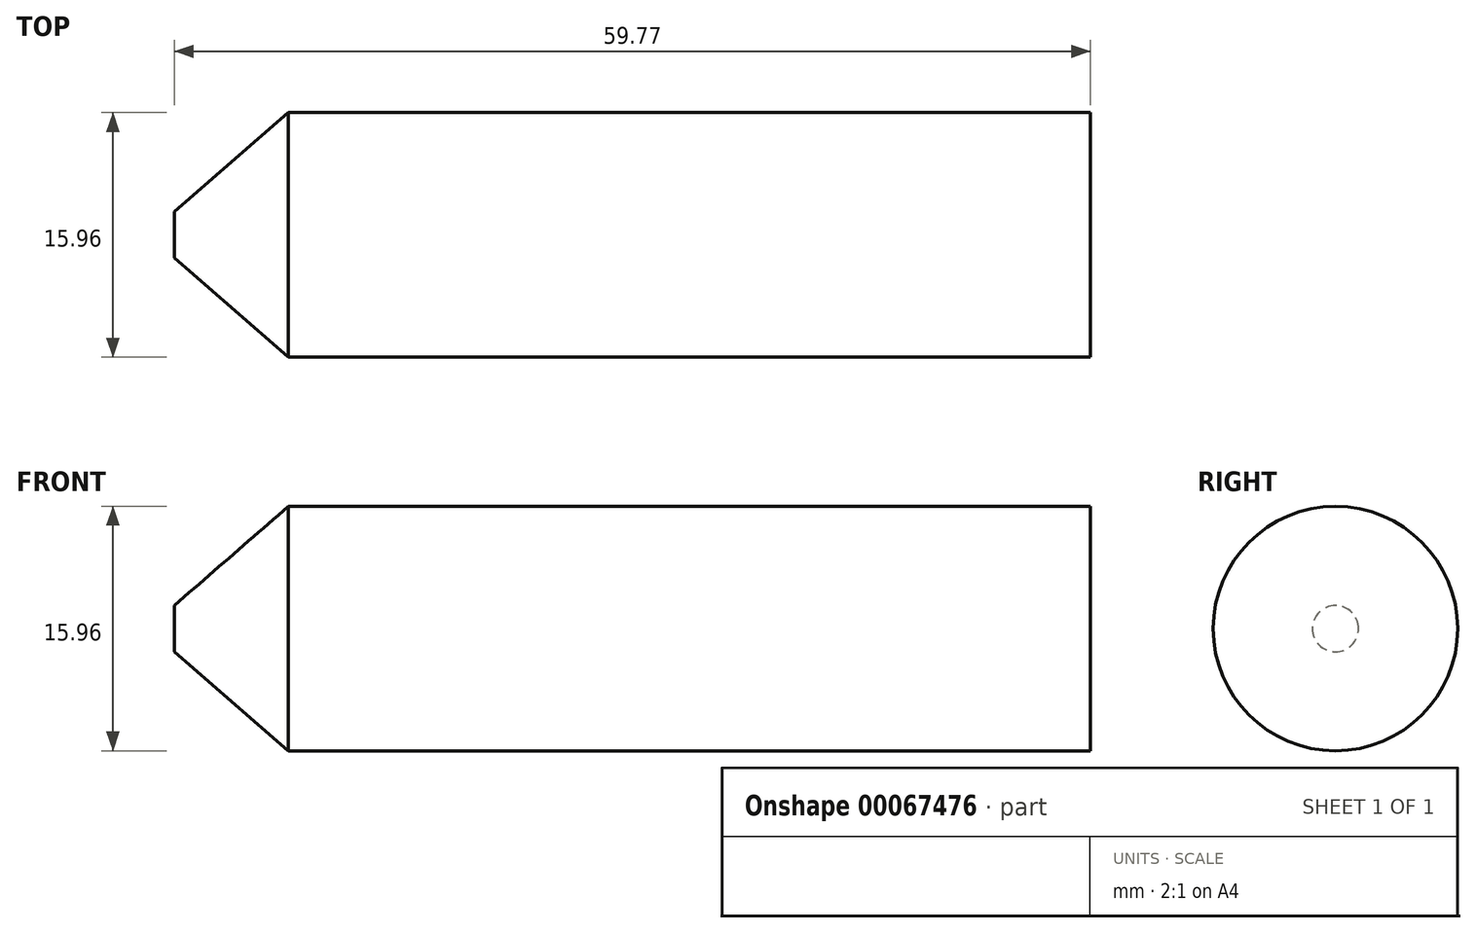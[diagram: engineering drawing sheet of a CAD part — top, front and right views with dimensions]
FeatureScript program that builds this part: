
annotation { "Feature Type Name" : "Feature", "Feature Type Description" : "" }
export const myFeature = defineFeature(function(context is Context, id is Id, definition is map)
    precondition{}
    {
        {
            var Q0;
            Q0=qCreatedBy(makeId("Front.planeOp"),FACE);
            var sketch = newSketch(context, id + "F0", { "sketchPlane" : qUnion([Q0])});
            skLineSegment(sketch, "E0.bottom", {"start": v(0, 0) * mm, "end": v(59.77, 0) * mm});
            skLineSegment(sketch, "E0.top", {"start": v(7.44, 7.98) * mm, "end": v(59.77, 7.98) * mm});
            skLineSegment(sketch, "E0.left", {"start": v(0, 0) * mm, "end": v(0, 1.5) * mm});
            skLineSegment(sketch, "E0.right", {"start": v(59.77, 0) * mm, "end": v(59.77, 7.98) * mm});
            skLineSegment(sketch, "E1", {"start": v(0, 1.5) * mm, "end": v(7.44, 7.98) * mm});
            skSolve(sketch);
        }
        {
            var Q0;
            Q0=makeQuery(id+"F0.imprint","IMPRINT",FACE,{"disambiguationData":[TD([[makeQuery(id+"F0.imprint","IMPRINT",EDGE,{"derivedFrom":sQuery(id+"F0.wireOp",EDGE,"E0.bottom")}),1.0]])]});
            var Q1;
            Q1=sQuery(id+"F0.wireOp",EDGE,"E0.bottom");
            revolve(context, id + "F1", {"entities" : qUnion([Q0]), "axis" : qUnion([Q1]), "revolveType" : RevolveType.FULL});
        }
    });
